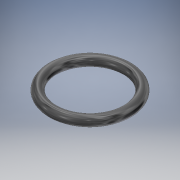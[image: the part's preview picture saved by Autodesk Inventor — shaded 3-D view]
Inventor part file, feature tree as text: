
AUTODESK INVENTOR PART (.ipt)
format: ipt  version: 2018 (Build 220112000, 112)  size: 171,520 bytes
history: native  units: mm (DEFAULTED — no unit token found)
features: revolve x1, sketch x1
ambient origin geometry x8: Origin, YZ Plane, XZ Plane, XY Plane, X Axis, Y Axis, Z Axis, Center Point
bodies: Solid1 (feature_tree)
feature tree (2):
  revolve  "Revolution1"  [1 undecoded]
  sketch  "Sketch2"  dims[d0=2.0mm d1=15.0mm d2=90.0deg]
note: 1 required parameter value undecoded (feature->parameter linkage not recoverable at this tier; creation-order binding heuristic only, values carry confidence <= 0.55)
